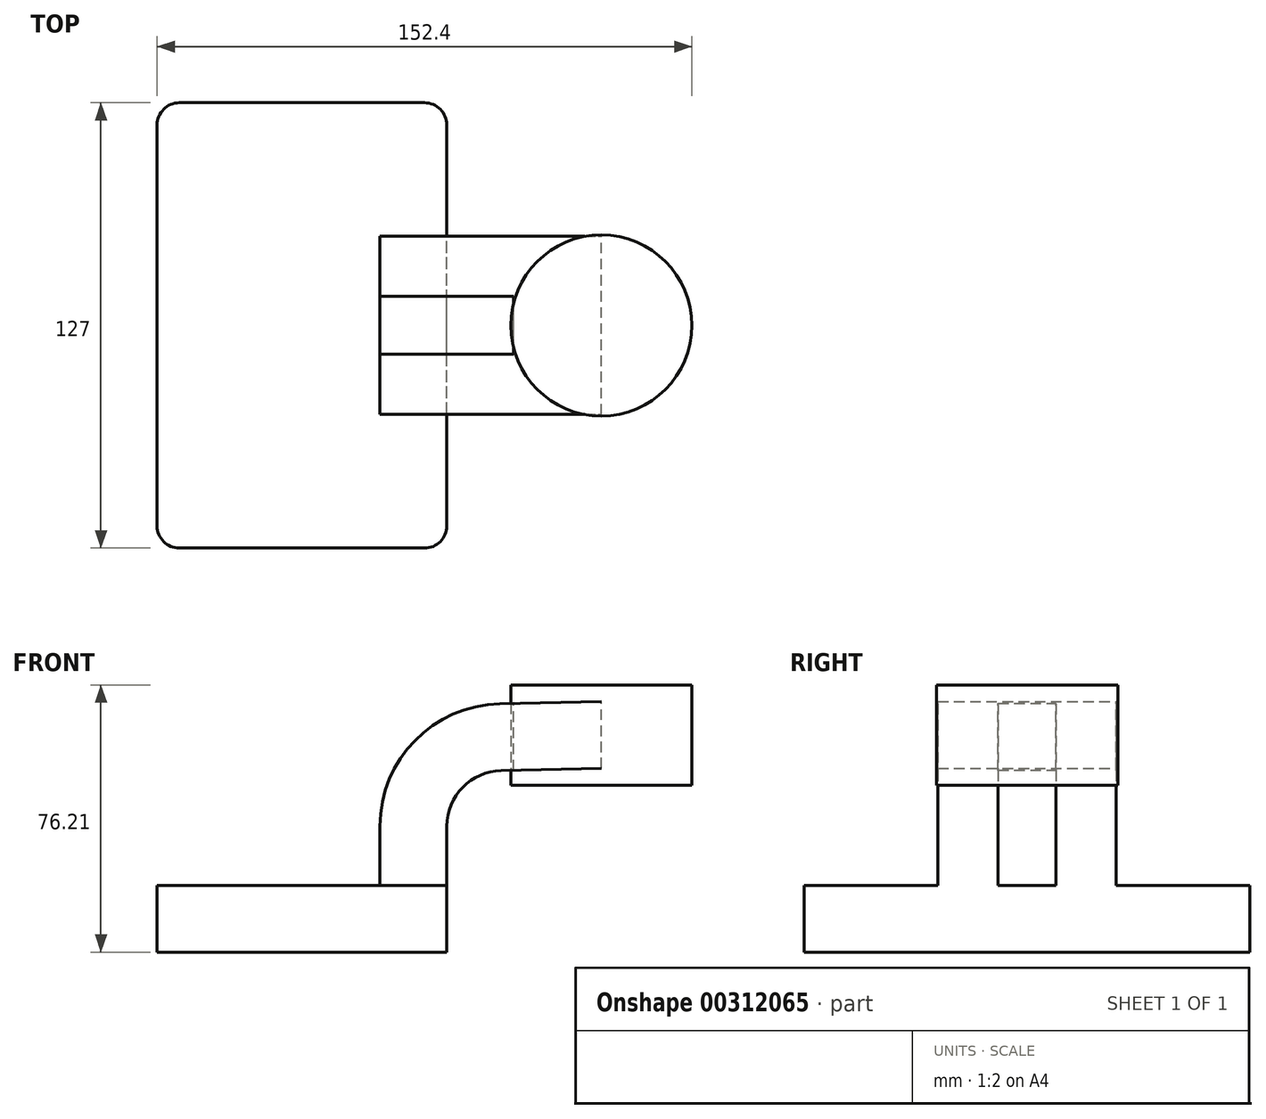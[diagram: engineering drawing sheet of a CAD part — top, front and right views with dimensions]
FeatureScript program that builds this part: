
annotation { "Feature Type Name" : "Feature", "Feature Type Description" : "" }
export const myFeature = defineFeature(function(context is Context, id is Id, definition is map)
    precondition{}
    {
        {
            var Q0;
            Q0=qCreatedBy(makeId("Front.planeOp"),FACE);
            var sketch = newSketch(context, id + "F0", { "sketchPlane" : qUnion([Q0])});
            skLineSegment(sketch, "E0.bottom", {"start": v(-41.28, 9.53) * mm, "end": v(41.28, 9.53) * mm});
            skLineSegment(sketch, "E0.top", {"start": v(-41.28, -9.52) * mm, "end": v(41.28, -9.52) * mm});
            skLineSegment(sketch, "E0.left", {"start": v(-41.28, 9.53) * mm, "end": v(-41.28, -9.52) * mm});
            skLineSegment(sketch, "E0.right", {"start": v(41.28, 9.53) * mm, "end": v(41.28, -9.52) * mm});
            skPoint(sketch, "E0.middle", {"position": v(0, 0) * mm});
            skLineSegment(sketch, "E1.bottom", {"start": v(111.12, 38.1) * mm, "end": v(60.32, 38.1) * mm});
            skLineSegment(sketch, "E1.top", {"start": v(111.12, 66.68) * mm, "end": v(60.32, 66.68) * mm});
            skLineSegment(sketch, "E1.left", {"start": v(111.12, 38.1) * mm, "end": v(111.12, 66.67) * mm});
            skLineSegment(sketch, "E1.right", {"start": v(60.32, 38.1) * mm, "end": v(60.32, 66.67) * mm});
            skPoint(sketch, "E1.middle", {"position": v(85.72, 52.39) * mm});
            skLineSegment(sketch, "E2", {"start": v(41.28, 9.53) * mm, "end": v(41.28, 26.37) * mm});
            skArc(sketch, "E3", {"start": v(41.28, 26.37) * mm, "mid": v(45.8, 37.47) * mm, "end": v(56.8, 42.24) * mm});
            skLineSegment(sketch, "E4", {"start": v(56.8, 42.24) * mm, "end": v(85.72, 42.88) * mm});
            skLineSegment(sketch, "E5.0", {"start": v(56.38, 61.28) * mm, "end": v(85.3, 61.92) * mm});
            skArc(sketch, "E5.1", {"start": v(22.23, 26.37) * mm, "mid": v(32.18, 50.8) * mm, "end": v(56.38, 61.28) * mm});
            skLineSegment(sketch, "E5.2", {"start": v(22.23, 9.53) * mm, "end": v(22.23, 26.37) * mm});
            skLineSegment(sketch, "E6", {"start": v(85.3, 38.1) * mm, "end": v(85.3, 66.68) * mm});
            skFitSpline(sketch, "E7", {"points": [v(-41.28, 9.52) * mm, v(60.32, 66.67) * mm], "startDerivative": vector(2.91, 101.71) * mm, "endDerivative": vector(128.71, 4.05) * mm});
            skSolve(sketch);
        }
        {
            var Q0;
            Q0=qCreatedBy(makeId("Front.planeOp"),FACE);
            var sketch = newSketch(context, id + "F1", { "sketchPlane" : qUnion([Q0])});
            skLineSegment(sketch, "E8.bottom", {"start": v(41.28, -9.52) * mm, "end": v(-41.28, -9.52) * mm});
            skLineSegment(sketch, "E8.top", {"start": v(41.27, 9.53) * mm, "end": v(-41.28, 9.53) * mm});
            skLineSegment(sketch, "E8.left", {"start": v(41.28, -9.52) * mm, "end": v(41.28, 9.53) * mm});
            skLineSegment(sketch, "E8.right", {"start": v(-41.28, -9.52) * mm, "end": v(-41.28, 9.53) * mm});
            skPoint(sketch, "E8.middle", {"position": v(0, 0) * mm});
            skLineSegment(sketch, "E9.bottom", {"start": v(111.12, 38.1) * mm, "end": v(60.32, 38.1) * mm});
            skLineSegment(sketch, "E9.top", {"start": v(111.13, 66.68) * mm, "end": v(60.32, 66.68) * mm});
            skLineSegment(sketch, "E9.left", {"start": v(111.13, 38.1) * mm, "end": v(111.13, 66.68) * mm});
            skLineSegment(sketch, "E9.right", {"start": v(60.32, 38.1) * mm, "end": v(60.32, 66.68) * mm});
            skPoint(sketch, "E9.middle", {"position": v(85.72, 52.39) * mm});
            skLineSegment(sketch, "E10", {"start": v(41.27, 9.53) * mm, "end": v(41.27, 52.72) * mm});
            skArc(sketch, "E11", {"start": v(41.27, 52.72) * mm, "mid": v(54.27, 68.33) * mm, "end": v(71.98, 58.37) * mm});
            skLineSegment(sketch, "E12", {"start": v(71.98, 58.37) * mm, "end": v(108.34, 58.37) * mm});
            skSolve(sketch);
        }
        {
            var Q0;
            Q0=makeQuery(id+"F1.imprint","IMPRINT",FACE,{"disambiguationData":[TD([[makeQuery(id+"F1.imprint","IMPRINT",EDGE,{"derivedFrom":sQuery(id+"F1.wireOp",EDGE,"E8.bottom")}),-1.0]])]});
            extrude(context, id + "F2", {"entities" : qUnion([Q0]), "endBound" : BoundingType.SYMMETRIC, "depth" : 127 * mm});
        }
        {
            var Q0;
            {var subQ1=sQuery(id+"F0.wireOp",EDGE,"E2");Q0=makeQuery(id+"F0.imprint","IMPRINT",FACE,{"disambiguationData":[TD([[makeQuery(id+"F0.imprint","IMPRINT",EDGE,{"derivedFrom":subQ1}),1.0]])]});}
            var Q1;
            {var subQ0=sQuery(id+"F0.wireOp",EDGE,"E4");var subQ1=sQuery(id+"F0.wireOp",EDGE,"E1.right");var subQ2=makeQuery(id+"F0.imprint","INTERSECT",VERTEX,{"derivedFrom":[subQ1,subQ0]});Q1=makeQuery(id+"F0.imprint","IMPRINT",FACE,{"disambiguationData":[TD([[makeQuery(id+"F0.imprint","IMPRINT",EDGE,{"disambiguationData":[TD([[subQ2,-1.0]])],"derivedFrom":subQ1}),-1.0]])]});}
            extrude(context, id + "F3", {"entities" : qUnion([Q0, Q1]), "operationType" : NewBodyOperationType.ADD, "endBound" : BoundingType.SYMMETRIC, "depth" : 50.8 * mm});
        }
        {
            var Q0;
            {var subQ0=sQuery(id+"F0.wireOp",EDGE,"E5.1");Q0=makeQuery(id+"F0.imprint","IMPRINT",FACE,{"disambiguationData":[TD([[makeQuery(id+"F0.imprint","IMPRINT",EDGE,{"derivedFrom":subQ0}),1.0]])]});}
            extrude(context, id + "F4", {"entities" : qUnion([Q0]), "endBound" : BoundingType.SYMMETRIC, "depth" : 16.5 * mm});
        }
        {
            var Q0;
            {var subQ4=sQuery(id+"F0.wireOp",EDGE,"E1.left");Q0=makeQuery(id+"F0.imprint","IMPRINT",FACE,{"disambiguationData":[TD([[makeQuery(id+"F0.imprint","IMPRINT",EDGE,{"derivedFrom":subQ4}),1.0]])]});}
            var Q1;
            Q1=sQuery(id+"F0.wireOp",EDGE,"E6");
            revolve(context, id + "F5", {"entities" : qUnion([Q0]), "axis" : qUnion([Q1]), "revolveType" : RevolveType.SYMMETRIC, "angle" : 360 * degree});
        }
        {
            var Q0;
            Q0=makeQuery(id+"F2.opExtrude","CAP_EDGE",EDGE,{"disambiguationData":[OSD([sQuery(id+"F1.wireOp",EDGE,"E8.right")])],"isStart":false});
            var Q1;
            Q1=makeQuery(id+"F2.opExtrude","CAP_EDGE",EDGE,{"disambiguationData":[OSD([sQuery(id+"F1.wireOp",EDGE,"E8.left")])],"isStart":false});
            var Q2;
            Q2=makeQuery(id+"F2.opExtrude","CAP_EDGE",EDGE,{"disambiguationData":[OSD([sQuery(id+"F1.wireOp",EDGE,"E8.left")])],"isStart":true});
            var Q3;
            Q3=makeQuery(id+"F2.opExtrude","CAP_EDGE",EDGE,{"disambiguationData":[OSD([sQuery(id+"F1.wireOp",EDGE,"E8.right")])],"isStart":true});
            fillet(context, id + "F6", {"entities" : qUnion([Q0, Q1, Q2, Q3]), "radius" : 6.35 * mm, "tangentPropagation" : true, "allowEdgeOverflow" : false});
        }
    });
